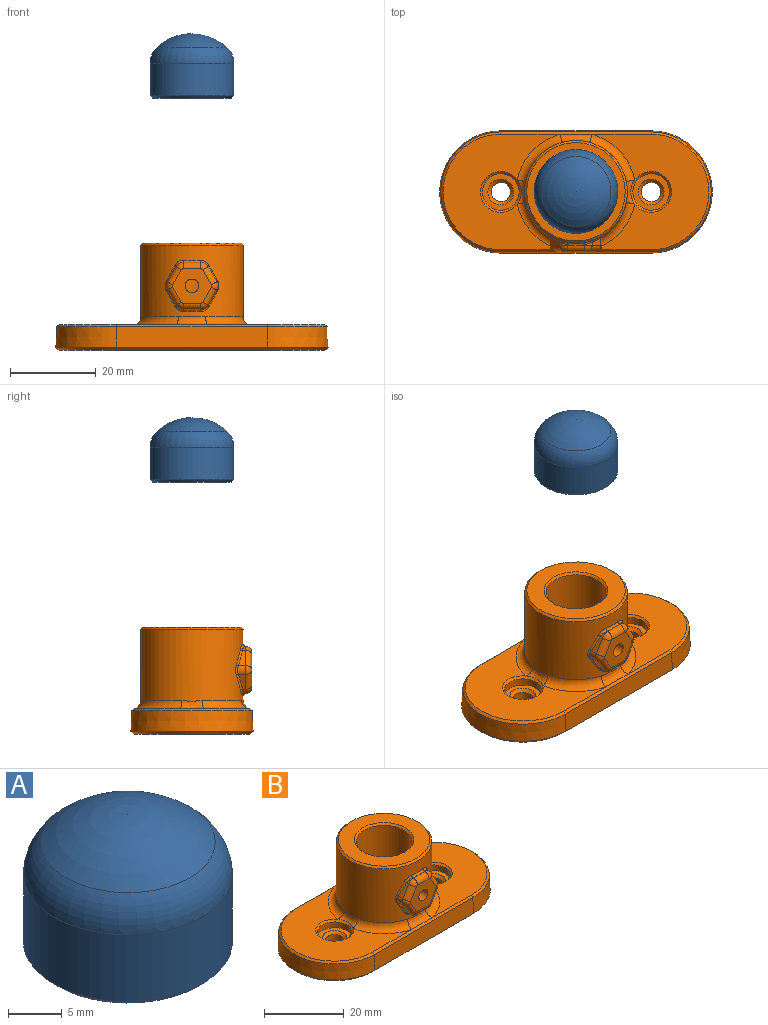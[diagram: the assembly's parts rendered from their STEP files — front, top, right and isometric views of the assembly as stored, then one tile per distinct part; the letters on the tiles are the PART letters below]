
ASSEMBLY  parts=2 mates=1
PART A: 8 faces, bbox 19.5x19.5x15 mm
  f0: plane 18.5x18.5mm, normal (0,0,-1), area 103.7mm2, adj f6,f7
  f1: cylinder r=6.75mm len=13.5mm, axis (0,0,-1), area 358.6mm2, adj f2,f6
  f2: plane 13.5x13.5mm, normal (0,0,-1), area 143.1mm2, adj f1
  f3: sphere r=12.01mm, area 239.9mm2, adj f5
  f4: cylinder r=9.75mm len=19.5mm, axis (0,0,-1), area 468.3mm2, adj f5,f7
  f5: torus R=4.75mm, axis (0,0,-1), area 238.7mm2, adj f3,f4
  f6: cone r=6.75mm half-angle=45deg, axis (0,0,-1), area 31.1mm2, adj f0,f1
  f7: cone r=9.25mm half-angle=45deg, axis (0,0,1), area 42.2mm2, adj f0,f4
PART B: 88 faces, bbox 63.5x32.2x25.1 mm
  f0: plane 27.25x26.9mm, normal (0,0,1), area 385.4mm2, adj f40,f43,f44,f45,f85,f86
  f1: plane 27.25x26.9mm, normal (0,0,1), area 385.4mm2, adj f41,f42,f43,f44,f81,f82
  f2: plane 2.02x0.17mm, normal (0,0,1), area 0.1mm2, adj f52,f56,f72
  f3: plane 2.02x0.17mm, normal (0,0,-1), area 0.1mm2, adj f55,f67,f75
  f4: cylinder r=6.95mm len=24mm, axis (0,0,-1), area 1015.8mm2, adj f26,f27,f28,f29,f30,f31,f39,f46
  f5: cylinder r=11.95mm len=23.9mm, axis (0,0,-1), area 1119mm2, adj f47,f68,f69,f70,f71,f72,f73,f74
  f6: plane 35x4.7mm, normal (0,1,0.05), area 164.7mm2, adj f7,f9,f36,f43
  f7: cone r=13.95mm half-angle=3deg, axis (0,0,-1), area 208.4mm2, adj f6,f8,f35,f42
  f8: plane 35x4.7mm, normal (0,-1,0.05), area 164.7mm2, adj f7,f9,f37,f44
  f9: cone r=13.95mm half-angle=3deg, axis (0,0,-1), area 208.4mm2, adj f6,f8,f38,f45
  f10: cylinder r=4.25mm len=8.5mm, axis (0,0,-1), area 46.7mm2, adj f14,f41
  f11: cylinder r=4.25mm len=8.5mm, axis (0,0,-1), area 46.7mm2, adj f16,f40
  f12: plane 61.9x26.9mm, normal (0,0,-1), area 1287.9mm2, adj f33,f34,f35,f36,f37,f38,f39
  f13: plane 22.9x22.9mm, normal (0,0,1), area 237.5mm2, adj f46,f47
  f14: plane 8.5x8.5mm, normal (0,0,1), area 28.5mm2, adj f10,f49
  f15: cylinder r=2.25mm len=4.5mm, axis (0,0,-1), area 35.3mm2, adj f34,f49
  f16: plane 8.5x8.5mm, normal (0,0,1), area 28.5mm2, adj f11,f48
  f17: cylinder r=2.25mm len=4.5mm, axis (0,0,-1), area 35.3mm2, adj f33,f48
  f18: plane 9.08x8mm, normal (0,-1,0), area 47.3mm2, adj f32,f56,f57,f58,f59,f60,f61,f62
  f19: plane 3.5x2.02mm, normal (0.87,0,-0.5), area 4.7mm2, adj f50,f51,f63,f79
  f20: plane 3.5x2.02mm, normal (0.87,0,0.5), area 4.7mm2, adj f51,f52,f59,f76
  f21: plane 2.02x0.17mm, normal (0,0,1), area 0.1mm2, adj f53,f56,f72
  f22: plane 3.5x2.02mm, normal (-0.87,0,0.5), area 4.7mm2, adj f53,f54,f60,f68
  f23: plane 2.02x0.17mm, normal (0,0,-1), area 0.1mm2, adj f50,f67,f75
  f24: plane 3.5x2.02mm, normal (-0.87,0,-0.5), area 4.7mm2, adj f54,f55,f64,f71
  f25: plane 6.93x6mm, normal (0,1,0), area 23.1mm2, adj f26,f27,f28,f29,f30,f31,f32
  f26: plane 5.51x3.08mm, normal (-0.87,0,0.5), area 17.4mm2, adj f4,f25,f27,f30
  f27: plane 5.51x3.08mm, normal (-0.87,0,-0.5), area 17.4mm2, adj f4,f25,f26,f28
  f28: plane 4.72x3.46mm, normal (0,0,-1), area 15.8mm2, adj f4,f25,f27,f29
  f29: plane 5.51x3.08mm, normal (0.87,0,-0.5), area 17.4mm2, adj f4,f25,f28,f31
  f30: plane 4.72x3.46mm, normal (0,0,1), area 15.8mm2, adj f4,f25,f26,f31
  f31: plane 5.51x3.08mm, normal (0.87,0,0.5), area 17.4mm2, adj f4,f25,f29,f30
  f32: cylinder r=1.6mm len=3.2mm, axis (0,1,0), area 25.1mm2, adj f18,f25
  f33: cone r=2.75mm half-angle=45deg, axis (0,0,-1), area 11.1mm2, adj f12,f17
  f34: cone r=2.75mm half-angle=45deg, axis (0,0,-1), area 11.1mm2, adj f12,f15
  f35: cone r=13.95mm half-angle=45deg, axis (0,0,1), area 47.6mm2, adj f7,f12,f36,f37
  f36: plane 35x0.77mm, normal (0,0.71,-0.71), area 38.3mm2, adj f6,f12,f35,f38
  f37: plane 35x0.77mm, normal (0,-0.71,-0.71), area 38.3mm2, adj f8,f12,f35,f38
  f38: cone r=13.45mm half-angle=45deg, axis (0,0,1), area 47.6mm2, adj f9,f12,f36,f37
  f39: cone r=7.45mm half-angle=45deg, axis (0,0,-1), area 32mm2, adj f4,f12
  f40: cone r=4.25mm half-angle=45deg, axis (0,0,1), area 20mm2, adj f0,f11,f87
  f41: cone r=4.25mm half-angle=45deg, axis (0,0,1), area 20mm2, adj f1,f10,f80
  f42: cone r=13.45mm half-angle=45deg, axis (0,0,-1), area 32.1mm2, adj f1,f7,f43,f44
  f43: plane 35.04x0.57mm, normal (0,0.71,0.71), area 26.1mm2, adj f0,f1,f6,f42,f45,f83
  f44: plane 35.04x0.57mm, normal (0,-0.71,0.71), area 26.1mm2, adj f0,f1,f8,f42,f45,f84
  f45: cone r=13.95mm half-angle=45deg, axis (0,0,-1), area 32.1mm2, adj f0,f9,f43,f44
  f46: cone r=6.95mm half-angle=45deg, axis (0,0,1), area 32mm2, adj f4,f13
  f47: cone r=11.45mm half-angle=45deg, axis (0,0,-1), area 52mm2, adj f5,f13
  f48: cone r=2.25mm half-angle=45deg, axis (0,0,1), area 17.5mm2, adj f16,f17
  f49: cone r=2.25mm half-angle=45deg, axis (0,0,1), area 17.5mm2, adj f14,f15
  f50: cylinder r=2mm len=1.73mm, axis (0,1,0), area 0.9mm2, adj f19,f23,f65,f77
  f51: cylinder r=2mm len=2mm, axis (0,1,0), area 3.5mm2, adj f19,f20,f61,f78
  f52: cylinder r=2mm len=1.73mm, axis (0,1,0), area 0.9mm2, adj f2,f20,f57,f74
  f53: cylinder r=2mm len=1.73mm, axis (0,1,0), area 0.9mm2, adj f21,f22,f58,f70
  f54: cylinder r=2mm len=2mm, axis (0,1,0), area 3.5mm2, adj f22,f24,f62,f69
  f55: cylinder r=2mm len=1.73mm, axis (0,1,0), area 0.9mm2, adj f3,f24,f66,f73
  f56: cylinder r=1.5mm len=4.04mm, axis (1,0,0), area 9.5mm2, adj f2,f18,f21,f57,f58
  f57: torus R=0.5mm, axis (0,1,0), area 3.6mm2, adj f18,f52,f56,f59
  f58: torus R=0.5mm, axis (0,1,0), area 3.6mm2, adj f18,f53,f56,f60
  f59: cylinder r=1.5mm len=4.25mm, axis (0.5,0,-0.87), area 9.5mm2, adj f18,f20,f57,f61
  f60: cylinder r=1.5mm len=4.25mm, axis (0.5,0,0.87), area 9.5mm2, adj f18,f22,f58,f62
  f61: torus R=0.5mm, axis (0,1,0), area 3.6mm2, adj f18,f51,f59,f63
  f62: torus R=0.5mm, axis (0,1,0), area 3.6mm2, adj f18,f54,f60,f64
  f63: cylinder r=1.5mm len=4.25mm, axis (-0.5,0,-0.87), area 9.5mm2, adj f18,f19,f61,f65
  f64: cylinder r=1.5mm len=4.25mm, axis (-0.5,0,0.87), area 9.5mm2, adj f18,f24,f62,f66
  f65: torus R=0.5mm, axis (0,1,0), area 3.6mm2, adj f18,f50,f63,f67
  f66: torus R=0.5mm, axis (0,1,0), area 3.6mm2, adj f18,f55,f64,f67
  f67: cylinder r=1.5mm len=4.04mm, axis (-1,0,0), area 9.5mm2, adj f3,f18,f23,f65,f66
  f68: bspline ~3.75x2.2mm, area 2.5mm2, adj f5,f22,f69,f70
  f69: bspline ~3.44x0.87mm, area 1.2mm2, adj f5,f54,f68,f71
  f70: bspline ~2.81x1.89mm, area 1.7mm2, adj f5,f53,f68,f72
  f71: bspline ~3.75x2.2mm, area 2.5mm2, adj f5,f24,f69,f73
  f72: torus R=12.45mm, axis (0,0,-1), area 3.1mm2, adj f2,f5,f21,f70,f74
  f73: bspline ~2.81x1.89mm, area 1.7mm2, adj f5,f55,f71,f75
  f74: bspline ~2.81x1.89mm, area 1.7mm2, adj f5,f52,f72,f76
  f75: torus R=12.45mm, axis (0,0,1), area 3.1mm2, adj f3,f5,f23,f73,f77
  f76: bspline ~3.75x2.2mm, area 2.5mm2, adj f5,f20,f74,f78
  f77: bspline ~2.81x1.89mm, area 1.7mm2, adj f5,f50,f75,f79
  f78: bspline ~3.44x0.87mm, area 1.2mm2, adj f5,f51,f76,f79
  f79: bspline ~3.75x2.2mm, area 2.5mm2, adj f5,f19,f77,f78
  f80: bspline ~5.95x2.26mm, area 11.5mm2, adj f5,f41,f81,f82
  f81: torus R=13.95mm, axis (0,0,1), area 43.8mm2, adj f1,f5,f80,f83
  f82: torus R=13.95mm, axis (0,0,1), area 43.8mm2, adj f1,f5,f80,f84
  f83: bspline ~9.17x2.38mm, area 18.9mm2, adj f5,f43,f81,f85
  f84: bspline ~9.17x2.38mm, area 18.9mm2, adj f5,f44,f82,f86
  f85: torus R=13.95mm, axis (0,0,1), area 43.8mm2, adj f0,f5,f83,f87
  f86: torus R=13.95mm, axis (0,0,1), area 43.8mm2, adj f0,f5,f84,f87
  f87: bspline ~5.61x2mm, area 11.5mm2, adj f5,f40,f85,f86
PLACE A t=(0,0,23.25)mm
PLACE B t=(0,0,-0.5)mm fixed
MATE slider B.f4 <-> A.f6  axis (0,0,1) through (0,0,24.5)mm
